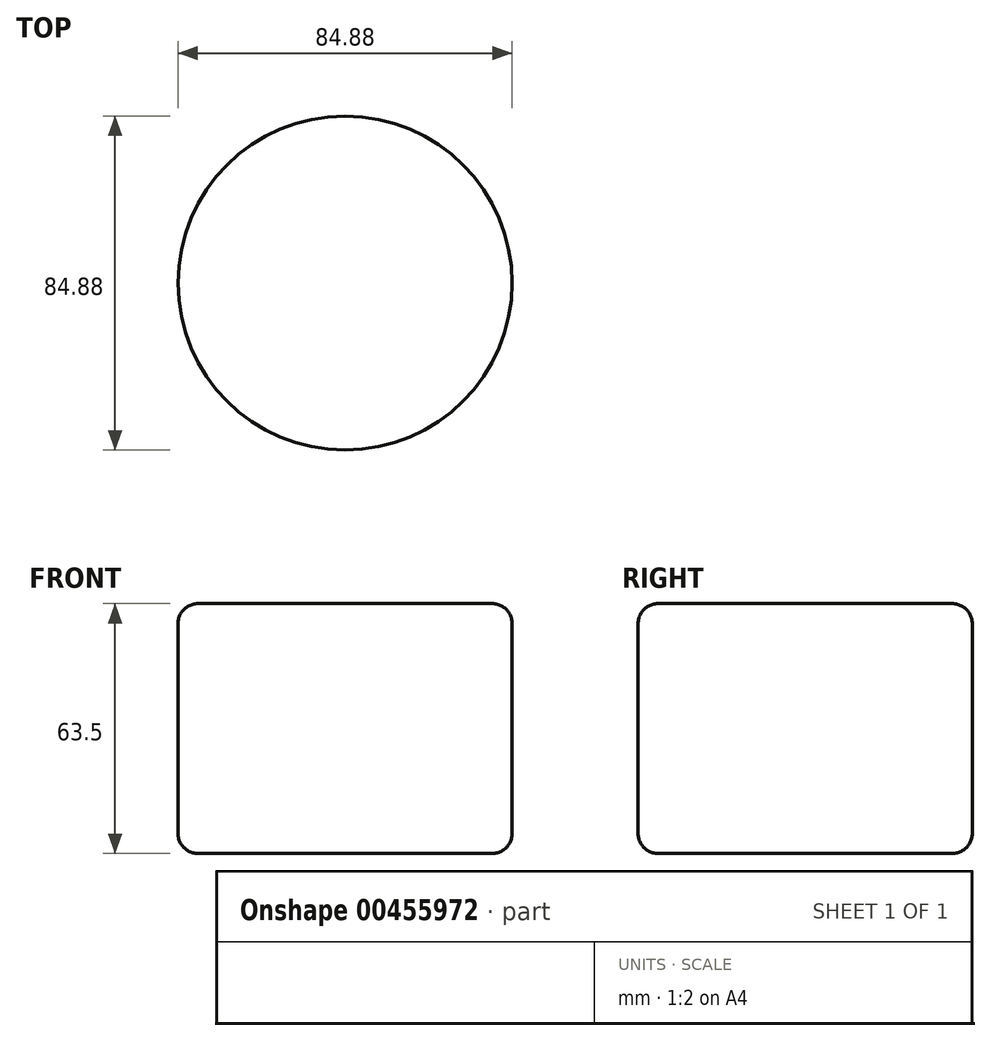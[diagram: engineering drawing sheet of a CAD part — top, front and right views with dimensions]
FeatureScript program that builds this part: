
annotation { "Feature Type Name" : "Feature", "Feature Type Description" : "" }
export const myFeature = defineFeature(function(context is Context, id is Id, definition is map)
    precondition{}
    {
        {
            var Q0;
            Q0=qCreatedBy(makeId("Top.planeOp"),FACE);
            var sketch = newSketch(context, id + "F0", { "sketchPlane" : qUnion([Q0])});
            skCircle(sketch, "E0", {"center": v(0, 0) * mm, "radius": 42.44 * mm});
            skSolve(sketch);
        }
        {
            var Q0;
            Q0 = qSketchRegion(id + "F0", true);
            extrude(context, id + "F1", {"entities" : qUnion([Q0]), "depth" : 63.5 * mm});
        }
        {
            var Q0;
            Q0=makeQuery(id+"F1.opExtrude","CAP_EDGE",EDGE,{"disambiguationData":[OSD([sQuery(id+"F0.wireOp",EDGE,"E0")])],"isStart":true});
            var Q1;
            Q1=makeQuery(id+"F1.opExtrude","CAP_FACE",FACE,{"disambiguationData":[OSD([sQuery(id+"F0.wireOp",EDGE,"E0")])],"isStart":false});
            fillet(context, id + "F2", {"entities" : qUnion([Q0, Q1]), "radius" : 5.08 * mm, "tangentPropagation" : true, "allowEdgeOverflow" : false});
        }
    });
